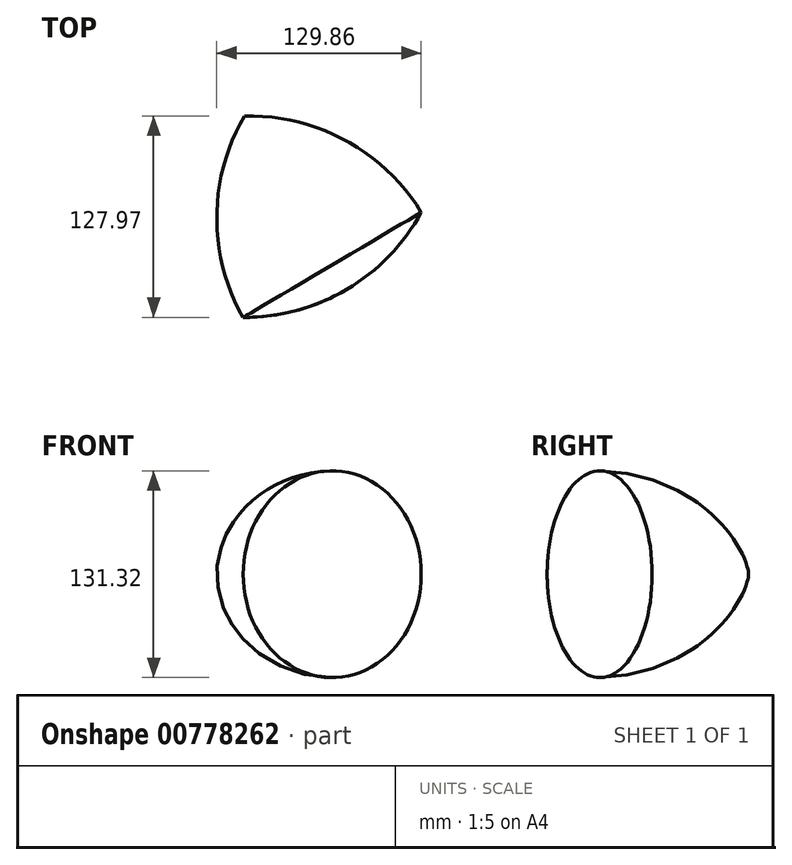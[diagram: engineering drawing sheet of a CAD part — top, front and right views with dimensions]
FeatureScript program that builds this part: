
annotation { "Feature Type Name" : "Feature", "Feature Type Description" : "" }
export const myFeature = defineFeature(function(context is Context, id is Id, definition is map)
    precondition{}
    {
        {
            var Q0;
            Q0=qCreatedBy(makeId("Top.planeOp"),FACE);
            var sketch = newSketch(context, id + "F0", { "sketchPlane" : qUnion([Q0])});
            skCircle(sketch, "E0.cCircle", {"center": v(0, 0) * mm, "radius": 36.93 * mm, "construction": true});
            skLineSegment(sketch, "E0.0", {"start": v(-36.52, 64.2) * mm, "end": v(73.86, -0.47) * mm});
            skLineSegment(sketch, "E0.1", {"start": v(73.86, -0.47) * mm, "end": v(-37.34, -63.73) * mm});
            skLineSegment(sketch, "E0.2", {"start": v(-37.34, -63.73) * mm, "end": v(-36.52, 64.2) * mm});
            skPoint(sketch, "E0.0.midPoint", {"position": v(18.67, 31.86) * mm});
            skCircle(sketch, "E1", {"center": v(-36.52, 64.2) * mm, "radius": 127.93 * mm});
            skCircle(sketch, "E2", {"center": v(73.86, -0.47) * mm, "radius": 127.93 * mm});
            skCircle(sketch, "E3", {"center": v(-37.34, -63.73) * mm, "radius": 127.93 * mm});
            skLineSegment(sketch, "E4", {"start": v(-36.52, 64.2) * mm, "end": v(28.44, -46.01) * mm});
            skSolve(sketch);
        }
        {
            var Q0;
            {var subQ1=sQuery(id+"F0.wireOp",EDGE,"E0.2");Q0=makeQuery(id+"F0.imprint","IMPRINT",FACE,{"disambiguationData":[TD([[makeQuery(id+"F0.imprint","IMPRINT",EDGE,{"derivedFrom":subQ1}),-1.0]])]});}
            var Q1;
            {var subQ0=sQuery(id+"F0.wireOp",EDGE,"E0.2");Q1=makeQuery(id+"F0.imprint","IMPRINT",FACE,{"disambiguationData":[TD([[makeQuery(id+"F0.imprint","IMPRINT",EDGE,{"derivedFrom":subQ0}),1.0]])]});}
            var Q2;
            {var subQ0=sQuery(id+"F0.wireOp",EDGE,"E1");var subQ3=sQuery(id+"F0.wireOp",EDGE,"E4");var subQ5=makeQuery(id+"F0.imprint","INTERSECT",VERTEX,{"derivedFrom":[subQ0,subQ3]});Q2=makeQuery(id+"F0.imprint","IMPRINT",FACE,{"disambiguationData":[TD([[makeQuery(id+"F0.imprint","IMPRINT",EDGE,{"disambiguationData":[TD([[subQ5,1.0]])],"derivedFrom":subQ3}),-1.0]])]});}
            var Q3;
            Q3=sQuery(id+"F0.wireOp",EDGE,"E4");
            revolve(context, id + "F1", {"surfaceOperationType" : NewSurfaceOperationType.NEW, "entities" : qUnion([Q0, Q1, Q2]), "axis" : qUnion([Q3]), "revolveType" : RevolveType.FULL});
        }
    });
